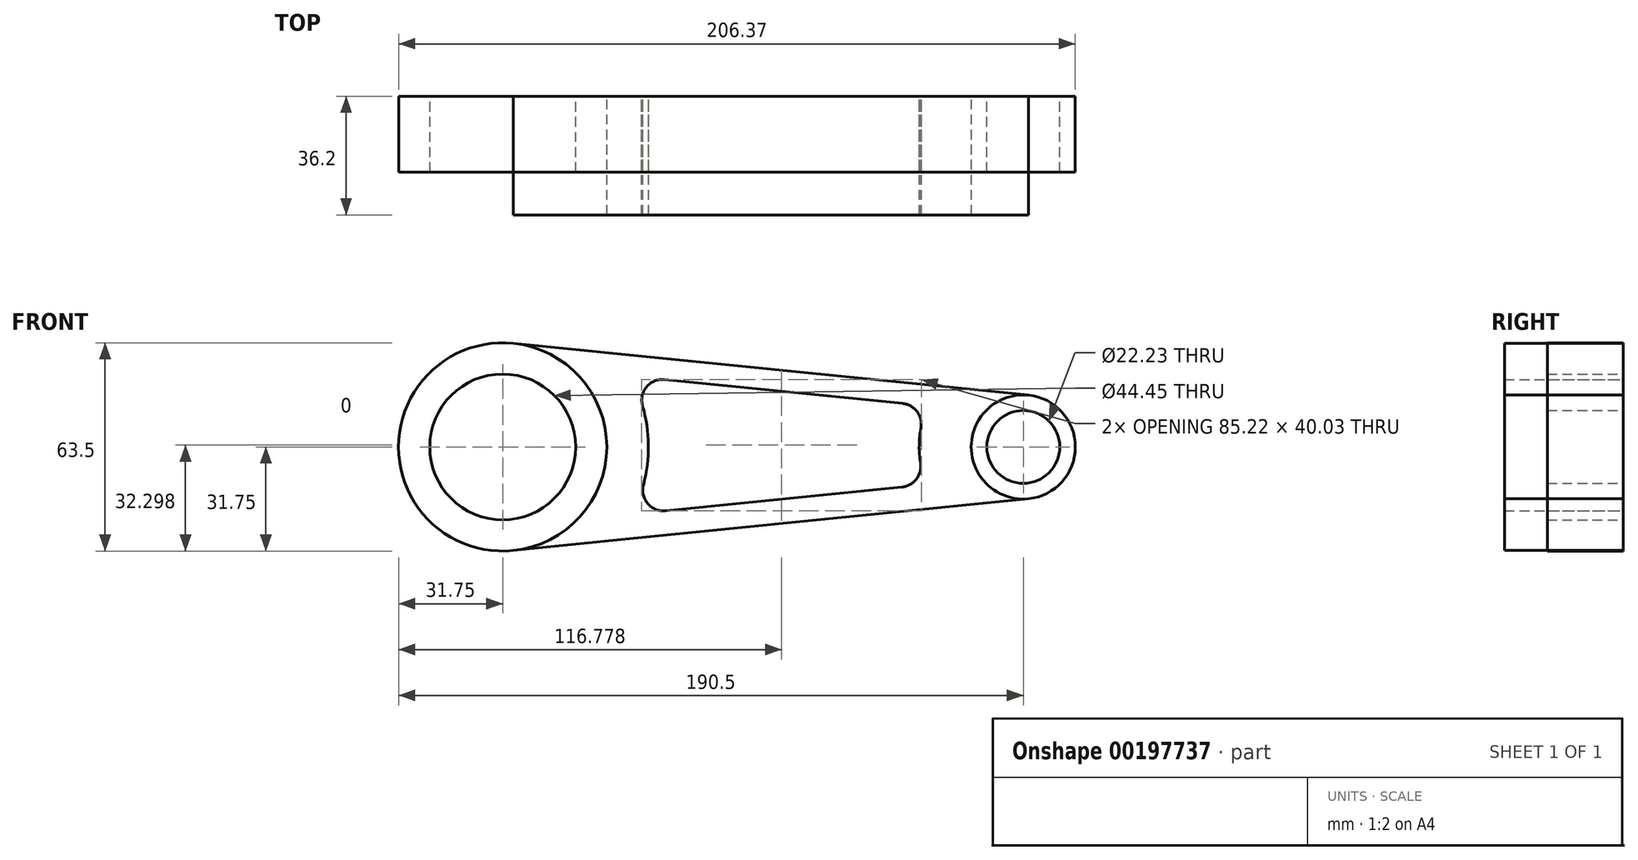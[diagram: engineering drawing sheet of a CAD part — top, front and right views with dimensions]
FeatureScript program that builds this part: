
annotation { "Feature Type Name" : "Feature", "Feature Type Description" : "" }
export const myFeature = defineFeature(function(context is Context, id is Id, definition is map)
    precondition{}
    {
        {
            var Q0;
            Q0=qCreatedBy(makeId("Front.planeOp"),FACE);
            var sketch = newSketch(context, id + "F0", { "sketchPlane" : qUnion([Q0])});
            skCircle(sketch, "E0", {"center": v(0, 0) * mm, "radius": 31.75 * mm});
            skCircle(sketch, "E1", {"center": v(158.75, 0) * mm, "radius": 15.88 * mm});
            skLineSegment(sketch, "E2", {"start": v(3.17, -31.6) * mm, "end": v(160.34, -15.8) * mm});
            skLineSegment(sketch, "E3", {"start": v(3.17, 31.6) * mm, "end": v(160.34, 15.8) * mm});
            skArc(sketch, "E4", {"start": v(42.67, 12.46) * mm, "mid": v(44.45, 0.5) * mm, "end": v(42.94, -11.5) * mm});
            skArc(sketch, "E5", {"start": v(127.53, 5.8) * mm, "mid": v(127, 0.44) * mm, "end": v(127.38, -4.92) * mm});
            skLineSegment(sketch, "E6.0", {"start": v(49.7, -19.47) * mm, "end": v(121.75, -12.23) * mm});
            skLineSegment(sketch, "E7.trimOffspring", {"start": v(49.4, 20.56) * mm, "end": v(121.93, 13.27) * mm});
            skPoint(sketch, "E8.visualSharp", {"position": v(38.84, 21.62) * mm});
            skArc(sketch, "E8.filletArc", {"start": v(49.4, 20.56) * mm, "mid": v(43.88, 18.3) * mm, "end": v(42.67, 12.46) * mm});
            skArc(sketch, "E9.filletArc", {"start": v(42.94, -11.5) * mm, "mid": v(44.23, -17.26) * mm, "end": v(49.7, -19.47) * mm});
            skArc(sketch, "E10.filletArc", {"start": v(127.53, 5.8) * mm, "mid": v(126.37, 10.77) * mm, "end": v(121.93, 13.27) * mm});
            skArc(sketch, "E11.filletArc", {"start": v(121.75, -12.23) * mm, "mid": v(126.14, -9.79) * mm, "end": v(127.38, -4.92) * mm});
            skCircle(sketch, "E12", {"center": v(0, 0) * mm, "radius": 22.23 * mm});
            skCircle(sketch, "E13", {"center": v(158.75, 0) * mm, "radius": 11.11 * mm});
            skSolve(sketch);
        }
        {
            var Q0;
            {var subQ0=sQuery(id+"F0.wireOp",EDGE,"E2");Q0=makeQuery(id+"F0.imprint","IMPRINT",FACE,{"disambiguationData":[TD([[makeQuery(id+"F0.imprint","IMPRINT",EDGE,{"derivedFrom":subQ0}),1.0]])]});}
            var Q1;
            Q1=makeQuery(id+"F0.imprint","IMPRINT",FACE,{"disambiguationData":[TD([[makeQuery(id+"F0.imprint","IMPRINT",EDGE,{"derivedFrom":sQuery(id+"F0.wireOp",EDGE,"E12")}),-1.0]])]});
            var Q2;
            Q2=makeQuery(id+"F0.imprint","IMPRINT",FACE,{"disambiguationData":[TD([[makeQuery(id+"F0.imprint","IMPRINT",EDGE,{"derivedFrom":sQuery(id+"F0.wireOp",EDGE,"E13")}),-1.0]])]});
            extrude(context, id + "F1", {"entities" : qUnion([Q0, Q1, Q2]), "depth" : 23.13 * mm});
        }
        {
            var Q0;
            {var subQ0=sQuery(id+"F0.wireOp",EDGE,"E2");Q0=makeQuery(id+"F0.imprint","IMPRINT",FACE,{"disambiguationData":[TD([[makeQuery(id+"F0.imprint","IMPRINT",EDGE,{"derivedFrom":subQ0}),1.0]])]});}
            extrude(context, id + "F2", {"entities" : qUnion([Q0]), "depth" : 36.2 * mm});
        }
    });
